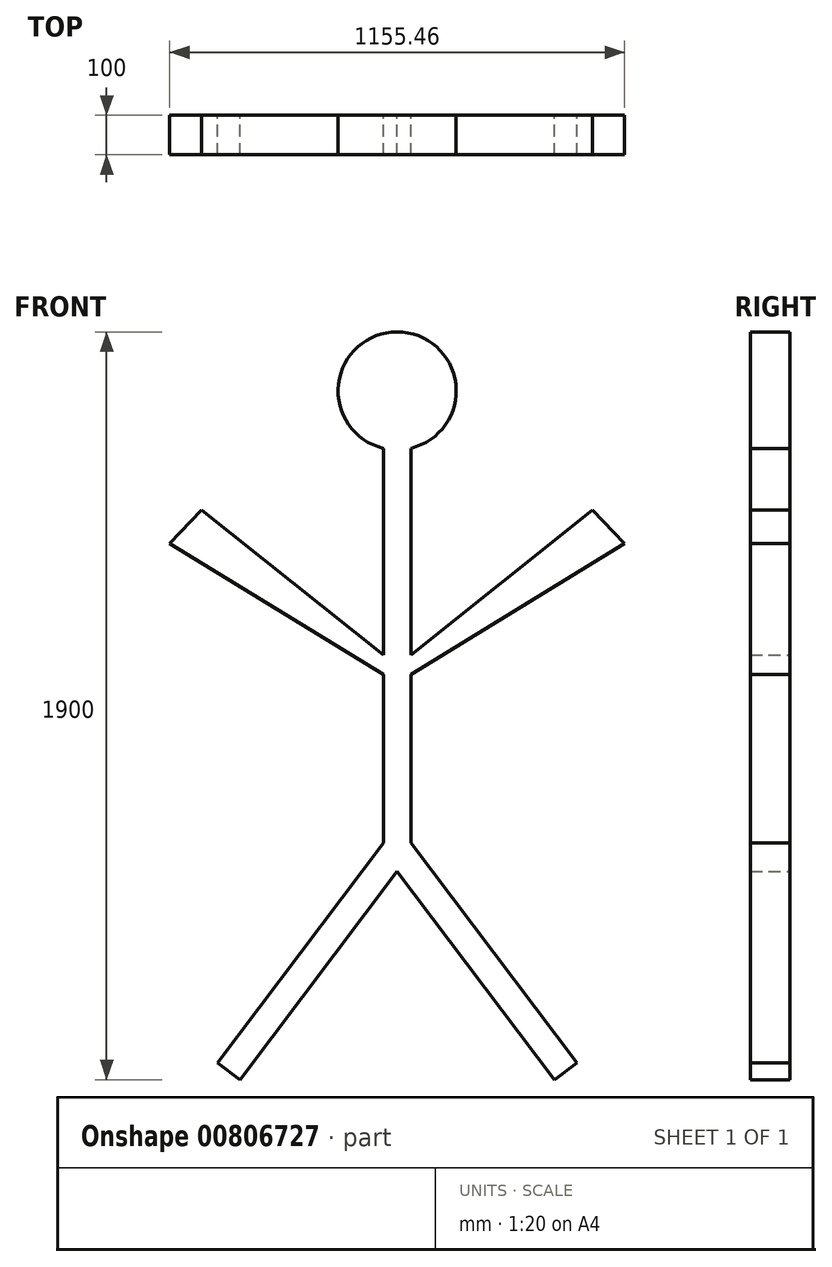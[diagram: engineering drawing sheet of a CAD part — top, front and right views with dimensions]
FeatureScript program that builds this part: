
annotation { "Feature Type Name" : "Feature", "Feature Type Description" : "" }
export const myFeature = defineFeature(function(context is Context, id is Id, definition is map)
    precondition{}
    {
        {
            var Q0;
            Q0=qCreatedBy(makeId("Front.planeOp"),FACE);
            var sketch = newSketch(context, id + "F0", { "sketchPlane" : qUnion([Q0])});
            skCircle(sketch, "E0", {"center": v(0, 1084.9) * mm, "radius": 150 * mm});
            skLineSegment(sketch, "E1", {"start": v(34.66, 938.95) * mm, "end": v(34.66, 414.45) * mm});
            skLineSegment(sketch, "E2", {"start": v(34.66, 414.45) * mm, "end": v(496.49, 782.2) * mm});
            skLineSegment(sketch, "E3", {"start": v(496.49, 782.2) * mm, "end": v(577.73, 697.13) * mm});
            skLineSegment(sketch, "E4", {"start": v(577.73, 697.13) * mm, "end": v(34.66, 364.6) * mm});
            skLineSegment(sketch, "E5", {"start": v(34.66, 364.6) * mm, "end": v(34.66, -64.05) * mm});
            skLineSegment(sketch, "E6", {"start": v(34.66, -64.05) * mm, "end": v(456.35, -622.06) * mm});
            skLineSegment(sketch, "E7", {"start": v(456.35, -622.06) * mm, "end": v(399.38, -665.1) * mm});
            skLineSegment(sketch, "E8", {"start": v(399.38, -665.1) * mm, "end": v(34.66, -182.49) * mm});
            skLineSegment(sketch, "E9", {"start": v(34.66, -182.49) * mm, "end": v(0, -136.62) * mm});
            skLineSegment(sketch, "E10.MirrorCS", {"start": v(-456.35, -622.06) * mm, "end": v(-399.38, -665.1) * mm});
            skLineSegment(sketch, "E11.MirrorCS", {"start": v(-496.49, 782.2) * mm, "end": v(-577.73, 697.13) * mm});
            skLineSegment(sketch, "E12.MirrorCS", {"start": v(-34.66, -182.49) * mm, "end": v(0, -136.62) * mm});
            skLineSegment(sketch, "E13.MirrorCS", {"start": v(-34.66, 938.95) * mm, "end": v(-34.66, 414.45) * mm});
            skLineSegment(sketch, "E14.MirrorCS", {"start": v(-34.66, 414.45) * mm, "end": v(-496.49, 782.2) * mm});
            skLineSegment(sketch, "E15.MirrorCS", {"start": v(-34.66, 364.6) * mm, "end": v(-34.66, -64.05) * mm});
            skLineSegment(sketch, "E16.MirrorCS", {"start": v(-34.66, -64.05) * mm, "end": v(-456.35, -622.06) * mm});
            skLineSegment(sketch, "E17.MirrorCS", {"start": v(-399.38, -665.1) * mm, "end": v(-34.66, -182.49) * mm});
            skLineSegment(sketch, "E18.MirrorCS", {"start": v(-577.73, 697.13) * mm, "end": v(-34.66, 364.6) * mm});
            skLineSegment(sketch, "E19", {"start": v(0, -136.62) * mm, "end": v(0, 1234.9) * mm, "construction": true});
            skSolve(sketch);
        }
        {
            var Q0;
            {var subQ0=sQuery(id+"F0.wireOp",EDGE,"E0");var subQ1=makeQuery(id+"F0.imprint","INTERSECT",VERTEX,{"derivedFrom":[subQ0,sQuery(id+"F0.wireOp",EDGE,"E1")]});Q0=makeQuery(id+"F0.imprint","IMPRINT",FACE,{"disambiguationData":[TD([[makeQuery(id+"F0.imprint","IMPRINT",EDGE,{"disambiguationData":[TD([[subQ1,1.0]])],"derivedFrom":subQ0}),1.0]])]});}
            var Q1;
            {var subQ0=sQuery(id+"F0.wireOp",EDGE,"E1");Q1=makeQuery(id+"F0.imprint","IMPRINT",FACE,{"disambiguationData":[TD([[makeQuery(id+"F0.imprint","IMPRINT",EDGE,{"derivedFrom":subQ0}),-1.0]])]});}
            extrude(context, id + "F1", {"entities" : qUnion([Q0, Q1]), "endBound" : BoundingType.SYMMETRIC, "depth" : 100 * mm, "offsetDistance" : 25 * mm});
        }
    });
